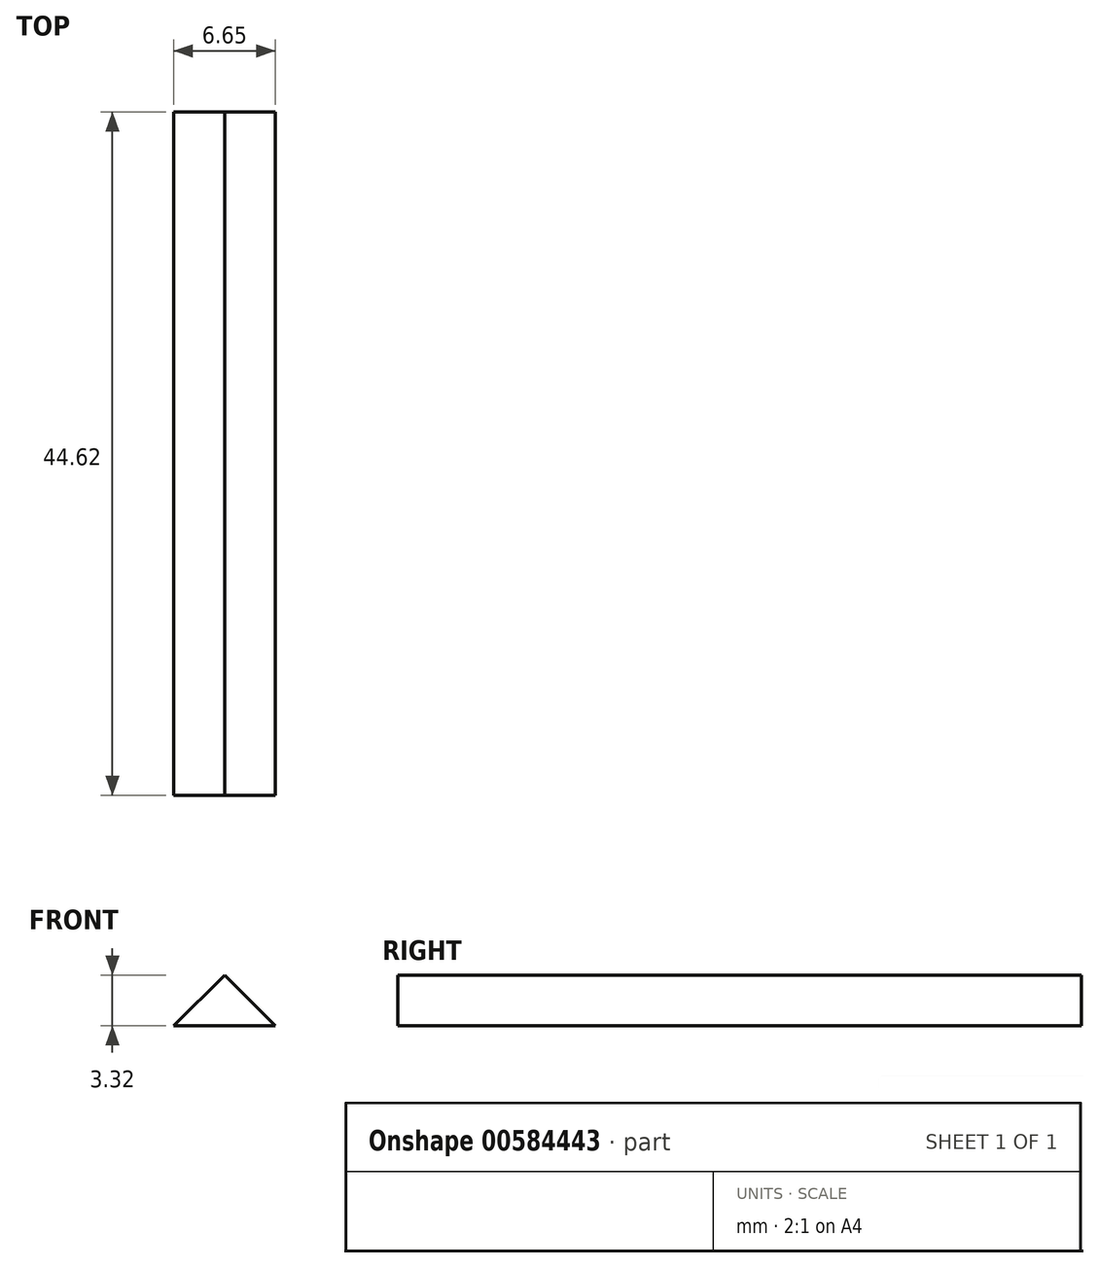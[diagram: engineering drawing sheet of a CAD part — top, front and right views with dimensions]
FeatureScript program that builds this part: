
annotation { "Feature Type Name" : "Feature", "Feature Type Description" : "" }
export const myFeature = defineFeature(function(context is Context, id is Id, definition is map)
    precondition{}
    {
        {
            var Q0;
            Q0=qCreatedBy(makeId("Front.planeOp"),FACE);
            var sketch = newSketch(context, id + "F0", { "sketchPlane" : qUnion([Q0])});
            skLineSegment(sketch, "E0", {"start": v(-50.78, -9.3) * mm, "end": v(-44.13, -9.3) * mm});
            skLineSegment(sketch, "E1", {"start": v(-50.78, -9.3) * mm, "end": v(-47.45, -5.98) * mm});
            skLineSegment(sketch, "E2", {"start": v(-47.45, -5.98) * mm, "end": v(-44.13, -9.3) * mm});
            skSolve(sketch);
        }
        {
            var Q0;
            Q0=makeQuery(id+"F0.imprint","IMPRINT",FACE,{"disambiguationData":[TD([[makeQuery(id+"F0.imprint","IMPRINT",EDGE,{"derivedFrom":sQuery(id+"F0.wireOp",EDGE,"E0")}),1.0]])]});
            extrude(context, id + "F1", {"entities" : qUnion([Q0]), "depth" : 44.62 * mm, "offsetDistance" : 25 * mm});
        }
    });
